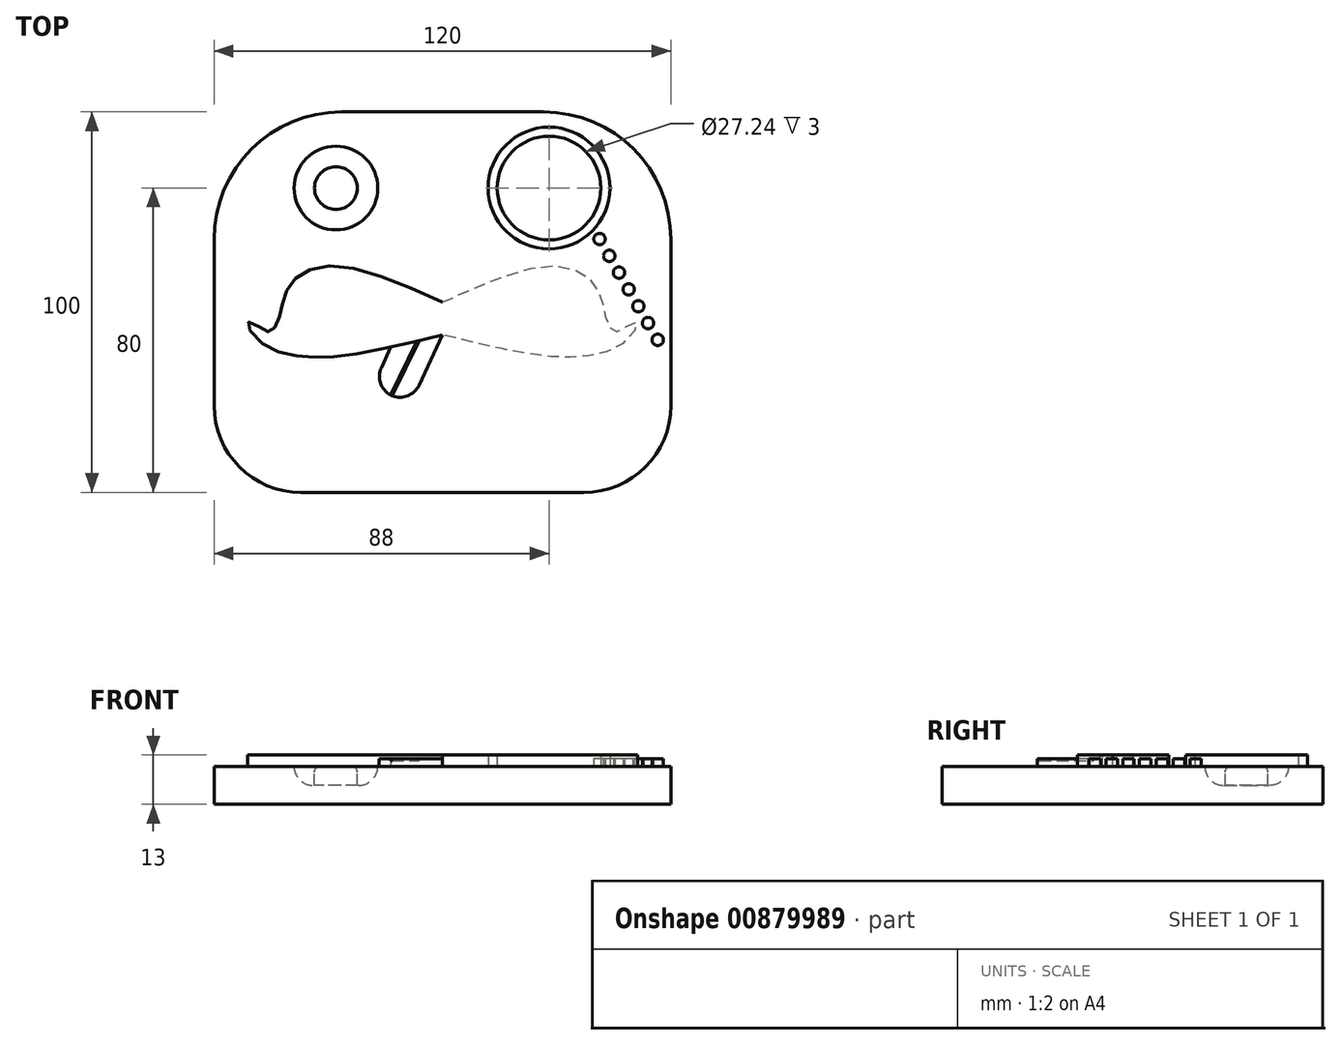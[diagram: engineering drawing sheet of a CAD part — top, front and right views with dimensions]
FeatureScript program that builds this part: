
annotation { "Feature Type Name" : "Feature", "Feature Type Description" : "" }
export const myFeature = defineFeature(function(context is Context, id is Id, definition is map)
    precondition{}
    {
        {
            var Q0;
            Q0=qCreatedBy(makeId("Top.planeOp"),FACE);
            var sketch = newSketch(context, id + "F0", { "sketchPlane" : qUnion([Q0])});
            skLineSegment(sketch, "E0.bottom", {"start": v(37.2, -50) * mm, "end": v(-37.2, -50) * mm});
            skLineSegment(sketch, "E0.top", {"start": v(26.57, 50) * mm, "end": v(-26.57, 50) * mm});
            skLineSegment(sketch, "E0.left", {"start": v(60, -27.2) * mm, "end": v(60, 16.57) * mm});
            skLineSegment(sketch, "E0.right", {"start": v(-60, -27.2) * mm, "end": v(-60, 16.57) * mm});
            skPoint(sketch, "E0.middle", {"position": v(0, 0) * mm});
            skPoint(sketch, "E1.visualSharp", {"position": v(-60, 50) * mm});
            skArc(sketch, "E1.filletArc", {"start": v(-26.57, 50) * mm, "mid": v(-50.2, 40.2) * mm, "end": v(-60, 16.57) * mm});
            skPoint(sketch, "E2.visualSharp", {"position": v(60, 50) * mm});
            skArc(sketch, "E2.filletArc", {"start": v(60, 16.57) * mm, "mid": v(50.2, 40.2) * mm, "end": v(26.57, 50) * mm});
            skPoint(sketch, "E3.visualSharp", {"position": v(-60, -50) * mm});
            skArc(sketch, "E3.filletArc", {"start": v(-60, -27.2) * mm, "mid": v(-53.32, -43.32) * mm, "end": v(-37.2, -50) * mm});
            skPoint(sketch, "E4.visualSharp", {"position": v(60, -50) * mm});
            skArc(sketch, "E4.filletArc", {"start": v(37.2, -50) * mm, "mid": v(53.32, -43.32) * mm, "end": v(60, -27.2) * mm});
            skSolve(sketch);
        }
        {
            var Q0;
            Q0=qSketchRegion(id+"F0",true);
            extrude(context, id + "F1", {"entities" : qUnion([Q0]), "depth" : 10 * mm});
        }
        {
            var Q0;
            Q0=makeQuery(id+"F1.opExtrude","CAP_FACE",FACE,{"disambiguationData":[OSD([sQuery(id+"F0.wireOp",EDGE,"E0.bottom"),sQuery(id+"F0.wireOp",EDGE,"E0.top"),sQuery(id+"F0.wireOp",EDGE,"E0.left"),sQuery(id+"F0.wireOp",EDGE,"E0.right"),sQuery(id+"F0.wireOp",EDGE,"E1.filletArc"),sQuery(id+"F0.wireOp",EDGE,"E2.filletArc"),sQuery(id+"F0.wireOp",EDGE,"E3.filletArc"),sQuery(id+"F0.wireOp",EDGE,"E4.filletArc")])],"isStart":false});
            cPlane(context, id + "F2", {"entities" : qUnion([Q0]), "cplaneType" : CPlaneType.OFFSET, "offset" : 0 * mm, "width" : 150 * mm, "height" : 150 * mm});
        }
        {
            var Q0;
            Q0=qCreatedBy(id+"F2.planeOp",FACE);
            var sketch = newSketch(context, id + "F3", { "sketchPlane" : qUnion([Q0])});
            skFitSpline(sketch, "E5", {"points": [v(0, 0) * mm, v(-28.4, 9.57) * mm, v(-38.75, 6) * mm, v(-41.96, 0) * mm, v(-43.27, -5.29) * mm, v(-45.4, -7.79) * mm, v(-47.3, -6.95) * mm, v(-51.11, -5.29) * mm, v(-48.14, -10.28) * mm, v(-38.28, -14.09) * mm, v(-26.03, -14.09) * mm, v(0, -8.62) * mm], "startDerivative": vector(-190.26, 85.43) * mm, "endDerivative": vector(183.95, 44.61) * mm});
            skLineSegment(sketch, "E6", {"start": v(0, 71.97) * mm, "end": v(0, -72.57) * mm, "construction": true});
            skFitSpline(sketch, "E7.MirrorCS", {"points": [v(0, 0) * mm, v(28.4, 9.57) * mm, v(38.75, 6) * mm, v(41.96, 0) * mm, v(43.27, -5.29) * mm, v(45.4, -7.79) * mm, v(47.3, -6.95) * mm, v(51.11, -5.29) * mm, v(48.14, -10.28) * mm, v(38.28, -14.09) * mm, v(26.03, -14.09) * mm, v(0, -8.62) * mm], "startDerivative": vector(190.26, 85.43) * mm, "endDerivative": vector(-183.95, 44.61) * mm});
            skSolve(sketch);
        }
        {
            var Q0;
            Q0=qSketchRegion(id+"F3",true);
            extrude(context, id + "F4", {"entities" : qUnion([Q0]), "operationType" : NewBodyOperationType.ADD, "depth" : 3 * mm});
        }
        {
            var Q0;
            Q0=qCreatedBy(id+"F2.planeOp",FACE);
            var sketch = newSketch(context, id + "F5", { "sketchPlane" : qUnion([Q0])});
            skLineSegment(sketch, "E8.bottom", {"start": v(-9.75, -3.6) * mm, "end": v(0.16, -8.23) * mm});
            skLineSegment(sketch, "E8.left", {"start": v(-9.75, -3.6) * mm, "end": v(-16.09, -17.2) * mm});
            skLineSegment(sketch, "E8.right", {"start": v(0.16, -8.23) * mm, "end": v(-6.18, -21.82) * mm});
            skLineSegment(sketch, "E9", {"start": v(0, 74.11) * mm, "end": v(0, -72.57) * mm, "construction": true});
            skArc(sketch, "E10", {"start": v(-16.09, -17.2) * mm, "mid": v(-13.44, -24.47) * mm, "end": v(-6.18, -21.82) * mm});
            skSolve(sketch);
        }
        {
            var Q0;
            Q0=qSketchRegion(id+"F5",true);
            extrude(context, id + "F6", {"entities" : qUnion([Q0]), "operationType" : NewBodyOperationType.ADD, "depth" : 2 * mm});
        }
        {
            var Q0;
            Q0=qCreatedBy(id+"F2.planeOp",FACE);
            var sketch = newSketch(context, id + "F7", { "sketchPlane" : qUnion([Q0])});
            skLineSegment(sketch, "E11", {"start": v(0, 80.6) * mm, "end": v(0, -78.54) * mm, "construction": true});
            skCircle(sketch, "E12", {"center": v(-28, 30) * mm, "radius": 11 * mm});
            skCircle(sketch, "E13", {"center": v(-28, 30) * mm, "radius": 5.62 * mm});
            skCircle(sketch, "E14.MirrorC", {"center": v(28, 30) * mm, "radius": 11 * mm});
            skCircle(sketch, "E15.MirrorC", {"center": v(28, 30) * mm, "radius": 5.62 * mm});
            skSolve(sketch);
        }
        {
            var Q0;
            Q0=makeQuery(id+"F7.imprint","IMPRINT",FACE,{"disambiguationData":[TD([[makeQuery(id+"F7.imprint","IMPRINT",EDGE,{"derivedFrom":sQuery(id+"F7.wireOp",EDGE,"E12")}),1.0]])]});
            var Q1;
            Q1=makeQuery(id+"F7.imprint","IMPRINT",FACE,{"disambiguationData":[TD([[makeQuery(id+"F7.imprint","IMPRINT",EDGE,{"derivedFrom":sQuery(id+"F7.wireOp",EDGE,"E14.MirrorC")}),-1.0]])]});
            var Q2;
            Q2=sQuery(id+"F7.wireOp",EDGE,"E12");
            extrude(context, id + "F8", {"entities" : qUnion([Q0, Q1]), "operationType" : NewBodyOperationType.REMOVE, "surfaceEntities" : qUnion([Q2]), "oppositeDirection" : true, "depth" : 5 * mm});
        }
        {
            var Q0;
            Q0=makeQuery(id+"F8.boolean.opBoolean","COPY",EDGE,{"derivedFrom":makeQuery(id+"F8.opExtrude","CAP_EDGE",EDGE,{"disambiguationData":[OSD([sQuery(id+"F7.wireOp",EDGE,"E12")])],"isStart":false})});
            var Q1;
            Q1=makeQuery(id+"F8.boolean.opBoolean","COPY",EDGE,{"derivedFrom":makeQuery(id+"F8.opExtrude","CAP_EDGE",EDGE,{"disambiguationData":[OSD([sQuery(id+"F7.wireOp",EDGE,"E14.MirrorC")])],"isStart":false})});
            fillet(context, id + "F9", {"entities" : qUnion([Q0, Q1]), "radius" : 5 * mm, "tangentPropagation" : true, "allowEdgeOverflow" : false});
        }
        {
            var Q0;
            Q0=makeQuery(id+"F8.boolean.opBoolean","COPY",EDGE,{"derivedFrom":makeQuery(id+"F8.opExtrude","CAP_EDGE",EDGE,{"disambiguationData":[OSD([sQuery(id+"F7.wireOp",EDGE,"E13")])],"isStart":true})});
            var Q1;
            Q1=makeQuery(id+"F8.boolean.opBoolean","COPY",EDGE,{"derivedFrom":makeQuery(id+"F8.opExtrude","CAP_EDGE",EDGE,{"disambiguationData":[OSD([sQuery(id+"F7.wireOp",EDGE,"E15.MirrorC")])],"isStart":true})});
            fillet(context, id + "F10", {"entities" : qUnion([Q0, Q1]), "radius" : 1.5 * mm, "tangentPropagation" : true, "allowEdgeOverflow" : false});
        }
        {
            var Q0;
            Q0=qCreatedBy(id+"F2.planeOp",FACE);
            var sketch = newSketch(context, id + "F11", { "sketchPlane" : qUnion([Q0])});
            skCircle(sketch, "E16", {"center": v(28, 30) * mm, "radius": 13.62 * mm});
            skCircle(sketch, "E17", {"center": v(28, 30) * mm, "radius": 16 * mm});
            skSolve(sketch);
        }
        {
            var Q0;
            Q0=makeQuery(id+"F11.imprint","IMPRINT",FACE,{"disambiguationData":[TD([[makeQuery(id+"F11.imprint","IMPRINT",EDGE,{"derivedFrom":sQuery(id+"F11.wireOp",EDGE,"E16")}),-1.0]])]});
            extrude(context, id + "F12", {"entities" : qUnion([Q0]), "operationType" : NewBodyOperationType.ADD, "depth" : 3 * mm});
        }
        {
            var Q0;
            Q0=qCreatedBy(id+"F2.planeOp",FACE);
            var sketch = newSketch(context, id + "F13", { "sketchPlane" : qUnion([Q0])});
            skCircle(sketch, "E18", {"center": v(41.27, 16.6) * mm, "radius": 1.5 * mm});
            skCircle(sketch, "E19.0.1.0", {"center": v(43.82, 12.18) * mm, "radius": 1.5 * mm});
            skCircle(sketch, "E19.0.2.0", {"center": v(46.37, 7.76) * mm, "radius": 1.5 * mm});
            skCircle(sketch, "E19.0.3.0", {"center": v(48.92, 3.35) * mm, "radius": 1.5 * mm});
            skCircle(sketch, "E19.0.4.0", {"center": v(51.47, -1.07) * mm, "radius": 1.5 * mm});
            skLineSegment(sketch, "E19.direction1", {"start": v(41.27, 16.6) * mm, "end": v(57.63, 16.6) * mm, "construction": true});
            skLineSegment(sketch, "E19.direction2", {"start": v(41.27, 16.6) * mm, "end": v(43.82, 12.18) * mm, "construction": true});
            skCircle(sketch, "E20.0.0.5", {"center": v(54.02, -5.49) * mm, "radius": 1.5 * mm});
            skCircle(sketch, "E20.0.0.6", {"center": v(56.57, -9.9) * mm, "radius": 1.5 * mm});
            skSolve(sketch);
        }
        {
            var Q0;
            Q0=qSketchRegion(id+"F13",true);
            var Q1;
            Q1=qConstructionFilter(qBodyType(qCreatedBy(id+"F13",EDGE),BodyType.WIRE),ConstructionObject.NO);
            extrude(context, id + "F14", {"entities" : qUnion([Q0]), "operationType" : NewBodyOperationType.ADD, "surfaceEntities" : qUnion([Q1]), "depth" : 2 * mm});
        }
        {
            var Q0;
            Q0=makeQuery(id+"F6.opExtrude","CAP_FACE",FACE,{"disambiguationData":[OSD([sQuery(id+"F5.wireOp",EDGE,"E8.bottom"),sQuery(id+"F5.wireOp",EDGE,"E8.left"),sQuery(id+"F5.wireOp",EDGE,"E8.right"),sQuery(id+"F5.wireOp",EDGE,"E10")])],"isStart":false});
            var sketch = newSketch(context, id + "F15", { "sketchPlane" : qUnion([Q0])});
            skLineSegment(sketch, "E21", {"start": v(-13.44, -24.47) * mm, "end": v(-6.5, -10.18) * mm});
            skLineSegment(sketch, "E22", {"start": v(-13.21, -24.57) * mm, "end": v(-6.18, -10.1) * mm});
            skLineSegment(sketch, "E23", {"start": v(-13.67, -24.36) * mm, "end": v(-6.8, -10.26) * mm});
            skSolve(sketch);
        }
        {
            var Q0;
            {var subQ0=sQuery(id+"F15.wireOp",EDGE,"E21");Q0=makeQuery(id+"F15.imprint","IMPRINT",FACE,{"disambiguationData":[TD([[makeQuery(id+"F15.imprint","IMPRINT",EDGE,{"derivedFrom":subQ0}),1.0]])]});}
            var Q1;
            {var subQ0=sQuery(id+"F15.wireOp",EDGE,"E21");Q1=makeQuery(id+"F15.imprint","IMPRINT",FACE,{"disambiguationData":[TD([[makeQuery(id+"F15.imprint","IMPRINT",EDGE,{"derivedFrom":subQ0}),-1.0]])]});}
            extrude(context, id + "F16", {"entities" : qUnion([Q0, Q1]), "operationType" : NewBodyOperationType.REMOVE, "oppositeDirection" : true, "depth" : .5 * mm});
        }
    });
